# Revit family: Shower_Arm-Modern-American_Standard-1660.241_Series
name_source: partatom
category: Plumbing Fixtures
units: mm (PartAtom-declared; Revit-internal decimal feet)

## family parameters
Cut with Voids When Loaded = No
Host = Face
OmniClass Number = 23.45.05.14.17
OmniClass Title = Showers
Part Type = Normal
Room Calculation Point = No
Round Connector Dimension = Use Diameter
Shared = Yes

## types (4) — shared parameters
Assembly Code = D2010700
CW Connection = Yes
CWFU = 3
Default Elevation = 78"
Description = Modern Shower Arm
HW Connection = Yes
HWFU = 3
Installation Type = Wall Mounted
Length = 5 1/2"
Manufacturer = American Standard
Price = Prices may vary. Please consult Manufacturer Representative for most up-to-date price list.
Product Documentation Link = https://www.americanstandard-us.com
Product Page URL = https://www.americanstandard-us.com
Revised Date = 05/12/2021
URL = https://www.americanstandard-us.com
Vent Connection = No
WFU = 4
Waste Connection = No
Water Connection Diameter = 1/2"
Water Connection Radius = 1/4"
Width = 2"

## per-type parameters (varying)
| type | Finish | Material | Model |
| 1660.241.002 | Brass-American Standard-002-Polished Chrome | Brass-American Standard-002-Polished Chrome | 1660.241.002 |
| 1660.241.295 | Brass-American Standard-295-Brushed Nickel | Brass-American Standard-295-Brushed Nickel | 1660.241.295 |
| 1660.2441.013 | Brass-American Standard-013-Polished Nickel | Brass-American Standard-013-Polished Nickel | 1660.241.013 |
| 1660.241.278 | Brass-American Standard-278-Legacy Bronze | Brass-American Standard-278-Legacy Bronze | 1660.241.278 |

## geometry (parser evidence)
native form markers: Sweep x3
no freeform markers — native parametric forms only
